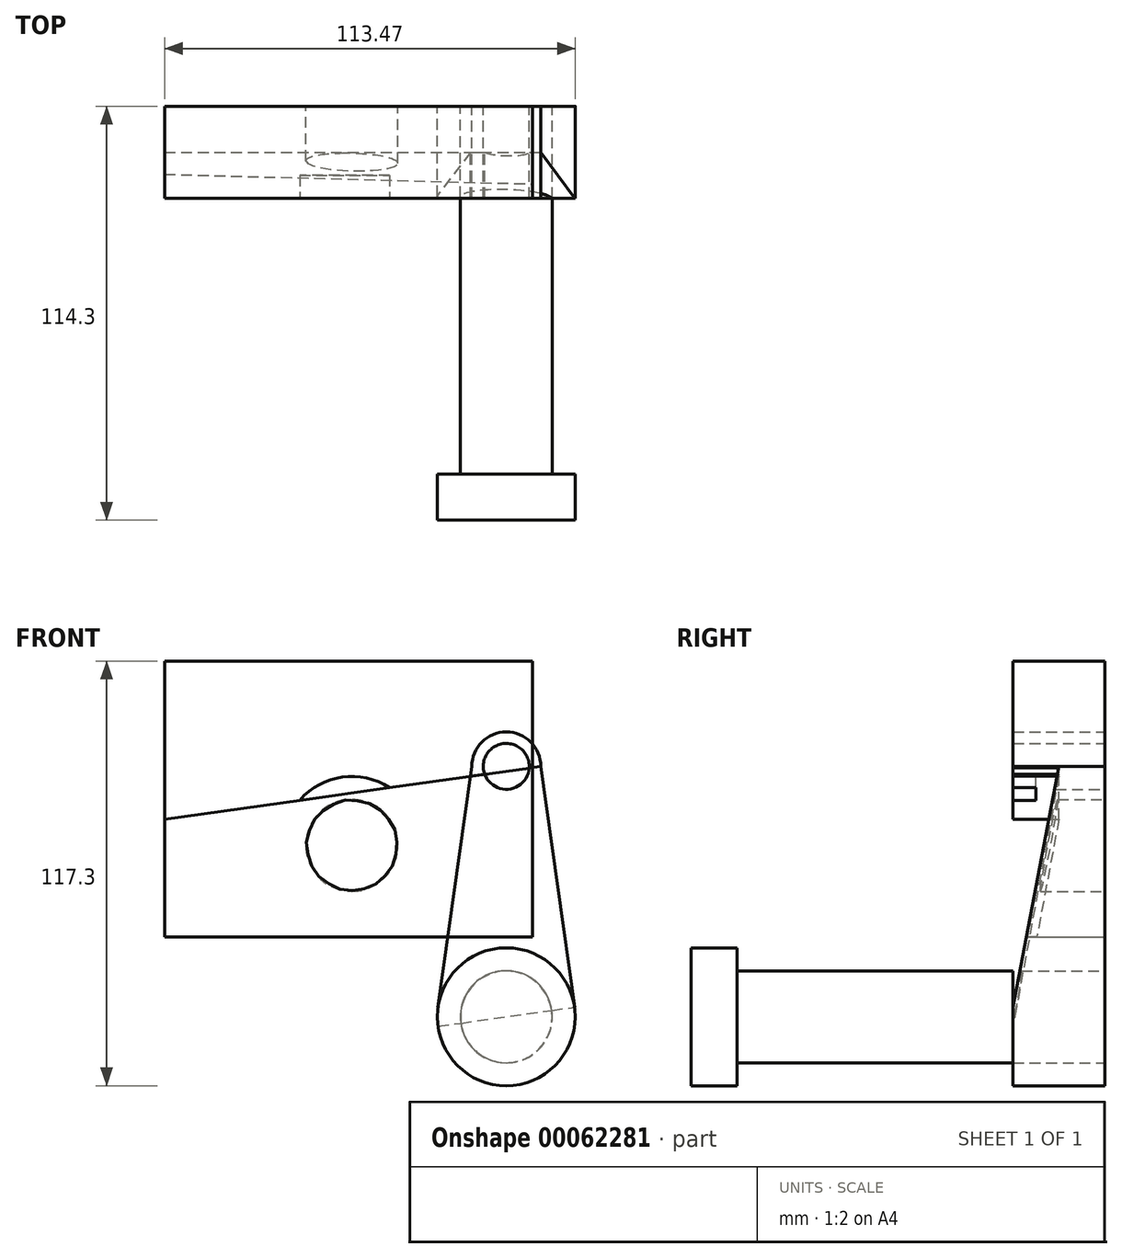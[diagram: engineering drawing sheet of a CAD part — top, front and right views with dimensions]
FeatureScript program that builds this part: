
annotation { "Feature Type Name" : "Feature", "Feature Type Description" : "" }
export const myFeature = defineFeature(function(context is Context, id is Id, definition is map)
    precondition{}
    {
        {
            var Q0;
            Q0=qCreatedBy(makeId("Front.planeOp"),FACE);
            var sketch = newSketch(context, id + "F0", { "sketchPlane" : qUnion([Q0])});
            skCircle(sketch, "E0", {"center": v(0, 0) * mm, "radius": 12.7 * mm});
            skSolve(sketch);
        }
        {
            var Q0;
            Q0 = qSketchRegion(id + "F0", true);
            extrude(context, id + "F1", {"entities" : qUnion([Q0]), "offsetDistance" : 25.4 * mm, "depth" : 101.6 * mm});
        }
        {
            var Q0;
            Q0=qCreatedBy(makeId("Front.planeOp"),FACE);
            var sketch = newSketch(context, id + "F2", { "sketchPlane" : qUnion([Q0])});
            skLineSegment(sketch, "E1.bottom", {"start": v(-94.42, 98.25) * mm, "end": v(7.18, 98.25) * mm});
            skLineSegment(sketch, "E1.top", {"start": v(-94.42, 22.05) * mm, "end": v(7.18, 22.05) * mm});
            skLineSegment(sketch, "E1.left", {"start": v(-94.42, 98.25) * mm, "end": v(-94.42, 22.05) * mm});
            skLineSegment(sketch, "E1.right", {"start": v(7.18, 98.25) * mm, "end": v(7.18, 22.05) * mm});
            skCircle(sketch, "E2", {"center": v(-42.66, 47.36) * mm, "radius": 12.7 * mm});
            skSolve(sketch);
        }
        {
            var Q0;
            Q0=makeQuery(id+"F2.imprint","IMPRINT",FACE,{"disambiguationData":[TD([[makeQuery(id+"F2.imprint","IMPRINT",EDGE,{"derivedFrom":sQuery(id+"F2.wireOp",EDGE,"E1.bottom")}),-1.0]])]});
            extrude(context, id + "F3", {"entities" : qUnion([Q0]), "offsetDistance" : 25.4 * mm, "depth" : 25.4 * mm});
        }
        {
            var Q0;
            Q0=makeQuery(id+"F1.opExtrude","CAP_FACE",FACE,{"disambiguationData":[OSD([sQuery(id+"F0.wireOp",EDGE,"E0")])],"isStart":false});
            var sketch = newSketch(context, id + "F4", { "sketchPlane" : qUnion([Q0])});
            skCircle(sketch, "E3", {"center": v(0, 0) * mm, "radius": 19.05 * mm});
            skSolve(sketch);
        }
        {
            var Q0;
            Q0 = qSketchRegion(id + "F4", true);
            extrude(context, id + "F5", {"entities" : qUnion([Q0]), "operationType" : NewBodyOperationType.ADD, "depth" : 12.7 * mm, "offsetDistance" : 25.4 * mm});
        }
        {
            var Q0;
            Q0=makeQuery(id+"F3.opExtrude","CAP_FACE",FACE,{"disambiguationData":[OSD([sQuery(id+"F2.wireOp",EDGE,"E1.bottom"),sQuery(id+"F2.wireOp",EDGE,"E1.top"),sQuery(id+"F2.wireOp",EDGE,"E1.left"),sQuery(id+"F2.wireOp",EDGE,"E1.right"),sQuery(id+"F2.wireOp",EDGE,"E2")])],"isStart":false});
            var sketch = newSketch(context, id + "F6", { "sketchPlane" : qUnion([Q0])});
            skCircle(sketch, "E4", {"center": v(-42.66, 47.36) * mm, "radius": 19.05 * mm});
            skSolve(sketch);
        }
        {
            var Q0;
            Q0 = qSketchRegion(id + "F6", true);
            extrude(context, id + "F7", {"entities" : qUnion([Q0]), "operationType" : NewBodyOperationType.REMOVE, "oppositeDirection" : true, "depth" : 6.35 * mm, "offsetDistance" : 25.4 * mm});
        }
        {
            var Q0;
            Q0=qCreatedBy(makeId("Front.planeOp"),FACE);
            var sketch = newSketch(context, id + "F8", { "sketchPlane" : qUnion([Q0])});
            skCircle(sketch, "E5", {"center": v(0, 0) * mm, "radius": 19.05 * mm});
            skCircle(sketch, "E6", {"center": v(0, 69.17) * mm, "radius": 9.53 * mm});
            skLineSegment(sketch, "E7", {"start": v(-9.52, 69.17) * mm, "end": v(-19.24, 0) * mm});
            skLineSegment(sketch, "E8", {"start": v(9.52, 69.17) * mm, "end": v(19.24, 0) * mm});
            skCircle(sketch, "E9", {"center": v(0, 69.17) * mm, "radius": 6.35 * mm});
            skCircle(sketch, "E10", {"center": v(0, 0) * mm, "radius": 12.7 * mm});
            skLineSegment(sketch, "E11", {"start": v(-16.69, 69.17) * mm, "end": v(22.4, 69.17) * mm});
            skLineSegment(sketch, "E12", {"start": v(-29.73, 0) * mm, "end": v(37.9, 0) * mm, "construction": true});
            skSolve(sketch);
        }
        {
            var Q0;
            Q0 = qSketchRegion(id + "F8", true);
            extrude(context, id + "F9", {"entities" : qUnion([Q0]), "depth" : 25.4 * mm, "offsetDistance" : 25.4 * mm});
        }
        {
            var Q0;
            Q0=makeQuery(id+"F9.opExtrude","SWEPT_FACE",FACE,{"disambiguationData":[OSD([sQuery(id+"F8.wireOp",EDGE,"E8")])]});
            var sketch = newSketch(context, id + "F10", { "sketchPlane" : qUnion([Q0])});
            skLineSegment(sketch, "E13", {"start": v(-12.7, 67.18) * mm, "end": v(-25.4, 0) * mm});
            skLineSegment(sketch, "E14", {"start": v(-12.7, 67.18) * mm, "end": v(-12.7, 77) * mm});
            skSolve(sketch);
        }
        {
            var Q0;
            {var subQ0=sQuery(id+"F10.wireOp",EDGE,"E13");Q0=makeQuery(id+"F10.imprint","IMPRINT",FACE,{"disambiguationData":[TD([[makeQuery(id+"F10.imprint","IMPRINT",EDGE,{"derivedFrom":subQ0}),-1.0]])]});}
            extrude(context, id + "F11", {"entities" : qUnion([Q0]), "operationType" : NewBodyOperationType.REMOVE, "endBound" : BoundingType.THROUGH_ALL, "oppositeDirection" : true, "depth" : 25.4 * mm, "offsetDistance" : 25.4 * mm});
        }
    });
